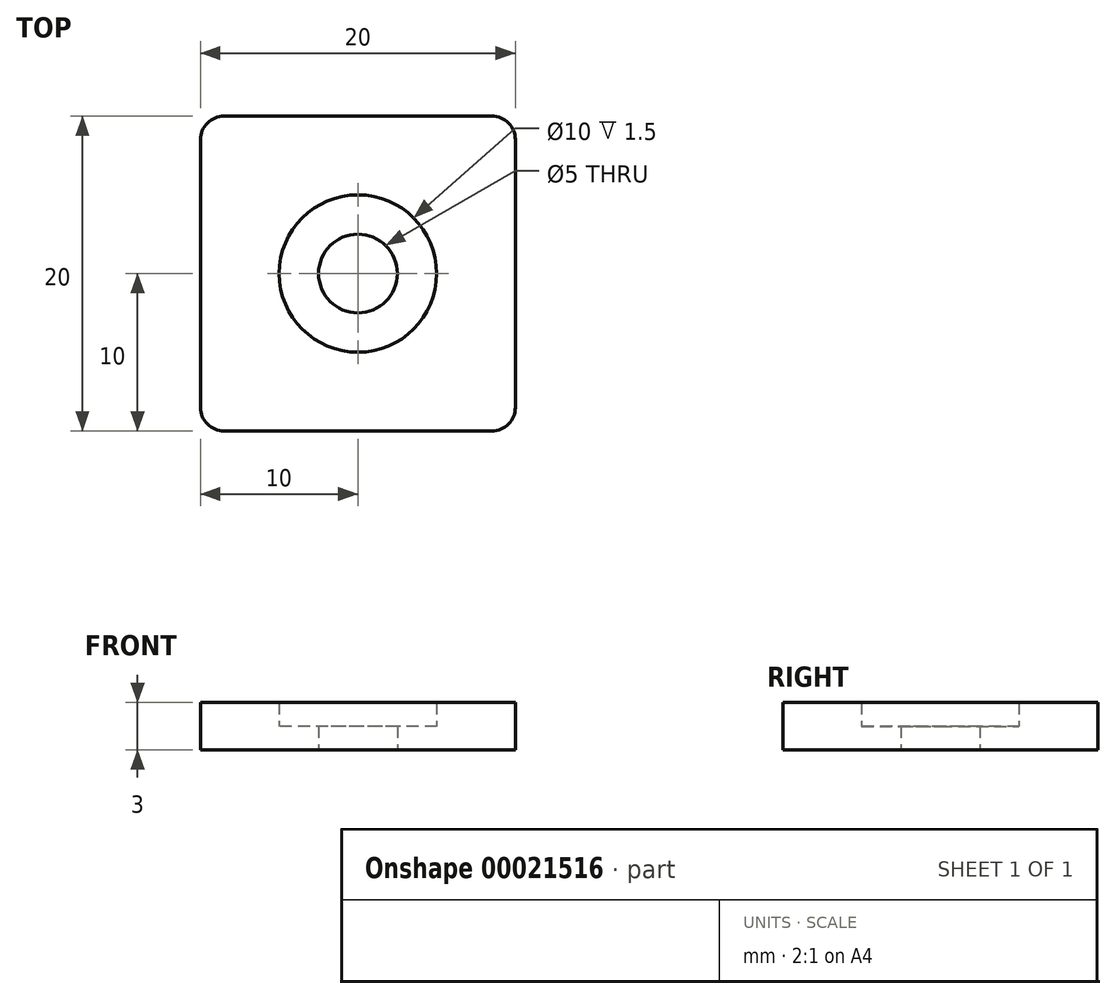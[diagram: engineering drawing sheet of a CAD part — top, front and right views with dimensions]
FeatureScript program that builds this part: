
annotation { "Feature Type Name" : "Feature", "Feature Type Description" : "" }
export const myFeature = defineFeature(function(context is Context, id is Id, definition is map)
    precondition{}
    {
        {
            var Q0;
            Q0=qCreatedBy(makeId("Top.planeOp"),FACE);
            var sketch = newSketch(context, id + "F0", { "sketchPlane" : qUnion([Q0])});
            skLineSegment(sketch, "E0.rect.bottom", {"start": v(10, 10) * mm, "end": v(-10, 10) * mm});
            skLineSegment(sketch, "E0.rect.top", {"start": v(10, -10) * mm, "end": v(-10, -10) * mm});
            skLineSegment(sketch, "E0.rect.left", {"start": v(10, 10) * mm, "end": v(10, -10) * mm});
            skLineSegment(sketch, "E0.rect.right", {"start": v(-10, 10) * mm, "end": v(-10, -10) * mm});
            skPoint(sketch, "E0.rect.middle", {"position": v(0, 0) * mm});
            skCircle(sketch, "E1", {"center": v(0, 0) * mm, "radius": 5 * mm});
            skCircle(sketch, "E2", {"center": v(0, 0) * mm, "radius": 2.5 * mm});
            skSolve(sketch);
        }
        {
            var Q0;
            Q0=makeQuery(id+"F0.imprint","IMPRINT",FACE,{"disambiguationData":[TD([[makeQuery(id+"F0.imprint","IMPRINT",EDGE,{"derivedFrom":sQuery(id+"F0.wireOp",EDGE,"E0.rect.bottom")}),1.0]])]});
            extrude(context, id + "F1", {"entities" : qUnion([Q0]), "depth" : 3 * mm});
        }
        {
            var Q0;
            Q0=makeQuery(id+"F0.imprint","IMPRINT",FACE,{"disambiguationData":[TD([[makeQuery(id+"F0.imprint","IMPRINT",EDGE,{"derivedFrom":sQuery(id+"F0.wireOp",EDGE,"E1")}),1.0]])]});
            extrude(context, id + "F2", {"entities" : qUnion([Q0]), "operationType" : NewBodyOperationType.ADD, "depth" : 1.5 * mm});
        }
        {
            var Q0;
            Q0=makeQuery(id+"F1.opExtrude","SWEPT_EDGE",EDGE,{"disambiguationData":[OSD([sQuery(id+"F0.wireOp",EDGE,"E0.rect.bottom"),sQuery(id+"F0.wireOp",EDGE,"E0.rect.right")])]});
            var Q1;
            Q1=makeQuery(id+"F1.opExtrude","SWEPT_EDGE",EDGE,{"disambiguationData":[OSD([sQuery(id+"F0.wireOp",EDGE,"E0.rect.top"),sQuery(id+"F0.wireOp",EDGE,"E0.rect.right")])]});
            var Q2;
            Q2=makeQuery(id+"F1.opExtrude","SWEPT_EDGE",EDGE,{"disambiguationData":[OSD([sQuery(id+"F0.wireOp",EDGE,"E0.rect.top"),sQuery(id+"F0.wireOp",EDGE,"E0.rect.left")])]});
            var Q3;
            Q3=makeQuery(id+"F1.opExtrude","SWEPT_EDGE",EDGE,{"disambiguationData":[OSD([sQuery(id+"F0.wireOp",EDGE,"E0.rect.bottom"),sQuery(id+"F0.wireOp",EDGE,"E0.rect.left")])]});
            fillet(context, id + "F3", {"entities" : qUnion([Q0, Q1, Q2, Q3]), "radius" : 1.5 * mm, "tangentPropagation" : true, "allowEdgeOverflow" : false});
        }
    });
